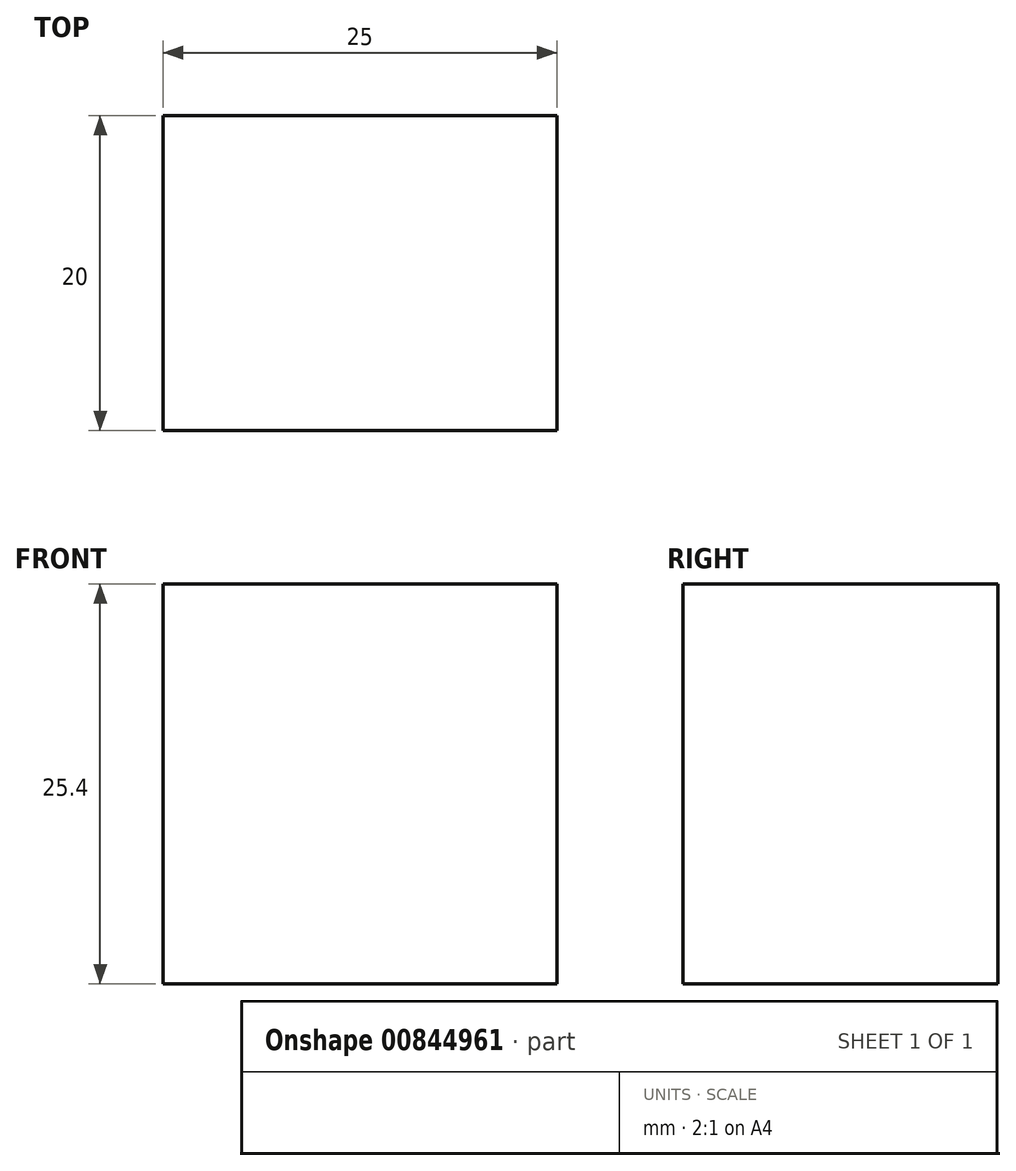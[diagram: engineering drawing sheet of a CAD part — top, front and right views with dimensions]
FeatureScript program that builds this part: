
annotation { "Feature Type Name" : "Feature", "Feature Type Description" : "" }
export const myFeature = defineFeature(function(context is Context, id is Id, definition is map)
    precondition{}
    {
        {
            var Q0;
            Q0=qCreatedBy(makeId("Top.planeOp"),FACE);
            var sketch = newSketch(context, id + "F0", { "sketchPlane" : qUnion([Q0])});
            skLineSegment(sketch, "E0.bottom", {"start": v(0, 0) * mm, "end": v(25, 0) * mm});
            skLineSegment(sketch, "E0.top", {"start": v(0, 20) * mm, "end": v(25, 20) * mm});
            skLineSegment(sketch, "E0.left", {"start": v(0, 0) * mm, "end": v(0, 20) * mm});
            skLineSegment(sketch, "E0.right", {"start": v(25, 0) * mm, "end": v(25, 20) * mm});
            skSolve(sketch);
        }
        {
            var Q0;
            Q0=makeQuery(id+"F0.imprint","IMPRINT",FACE,{"disambiguationData":[TD([[makeQuery(id+"F0.imprint","IMPRINT",EDGE,{"derivedFrom":sQuery(id+"F0.wireOp",EDGE,"E0.bottom")}),1.0]])]});
            extrude(context, id + "F1", {"entities" : qUnion([Q0]), "depth" : 25.4 * mm, "offsetDistance" : 25.4 * mm});
        }
    });
